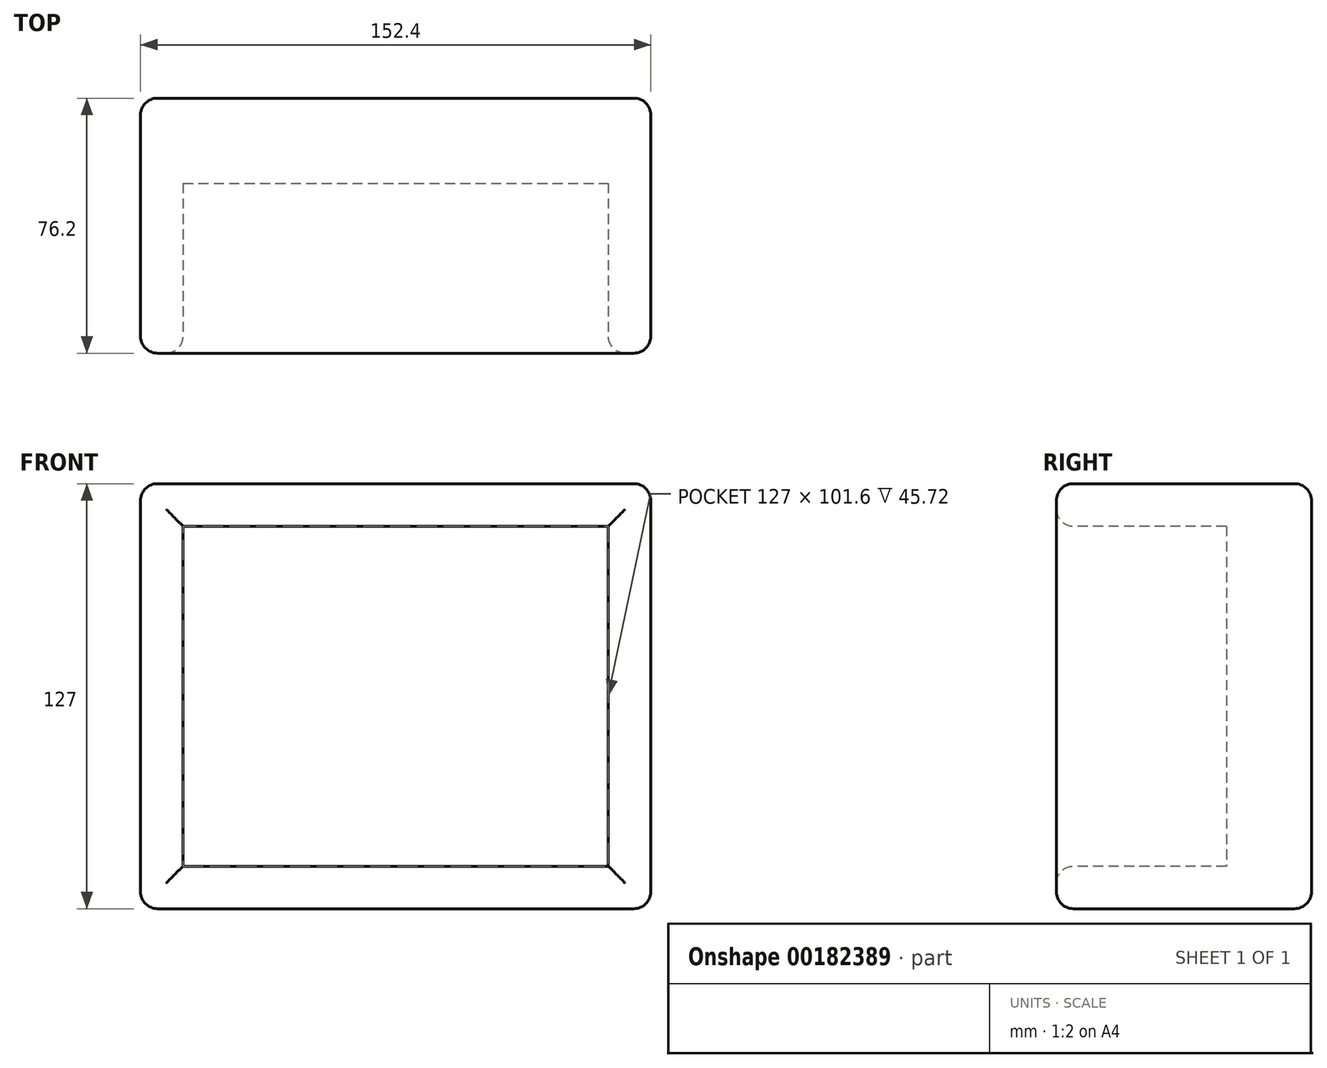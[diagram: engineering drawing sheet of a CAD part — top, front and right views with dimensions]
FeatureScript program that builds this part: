
annotation { "Feature Type Name" : "Feature", "Feature Type Description" : "" }
export const myFeature = defineFeature(function(context is Context, id is Id, definition is map)
    precondition{}
    {
        {
            var Q0;
            Q0=qCreatedBy(makeId("Front.planeOp"),FACE);
            var sketch = newSketch(context, id + "F0", { "sketchPlane" : qUnion([Q0])});
            skLineSegment(sketch, "E0.bottom", {"start": v(76.2, -63.5) * mm, "end": v(-76.2, -63.5) * mm});
            skLineSegment(sketch, "E0.top", {"start": v(76.2, 63.5) * mm, "end": v(-76.2, 63.5) * mm});
            skLineSegment(sketch, "E0.left", {"start": v(76.2, -63.5) * mm, "end": v(76.2, 63.5) * mm});
            skLineSegment(sketch, "E0.right", {"start": v(-76.2, -63.5) * mm, "end": v(-76.2, 63.5) * mm});
            skPoint(sketch, "E0.middle", {"position": v(0, 0) * mm});
            skSolve(sketch);
        }
        {
            var Q0;
            Q0=makeQuery(id+"F0.imprint","IMPRINT",FACE,{"disambiguationData":[TD([[makeQuery(id+"F0.imprint","IMPRINT",EDGE,{"derivedFrom":sQuery(id+"F0.wireOp",EDGE,"E0.bottom")}),-1.0]])]});
            extrude(context, id + "F1", {"entities" : qUnion([Q0]), "oppositeDirection" : true, "depth" : 76.2 * mm});
        }
        {
            var Q0;
            Q0=makeQuery(id+"F1.opExtrude","CAP_FACE",FACE,{"disambiguationData":[OSD([sQuery(id+"F0.wireOp",EDGE,"E0.bottom"),sQuery(id+"F0.wireOp",EDGE,"E0.top"),sQuery(id+"F0.wireOp",EDGE,"E0.left"),sQuery(id+"F0.wireOp",EDGE,"E0.right")])],"isStart":true});
            var sketch = newSketch(context, id + "F2", { "sketchPlane" : qUnion([Q0])});
            skLineSegment(sketch, "E1.bottom", {"start": v(-63.5, 50.8) * mm, "end": v(63.5, 50.8) * mm});
            skLineSegment(sketch, "E1.top", {"start": v(-63.5, -50.8) * mm, "end": v(63.5, -50.8) * mm});
            skLineSegment(sketch, "E1.left", {"start": v(-63.5, 50.8) * mm, "end": v(-63.5, -50.8) * mm});
            skLineSegment(sketch, "E1.right", {"start": v(63.5, 50.8) * mm, "end": v(63.5, -50.8) * mm});
            skPoint(sketch, "E1.middle", {"position": v(0, 0) * mm});
            skSolve(sketch);
        }
        {
            var Q0;
            Q0=makeQuery(id+"F2.imprint","IMPRINT",FACE,{"disambiguationData":[TD([[makeQuery(id+"F2.imprint","IMPRINT",EDGE,{"derivedFrom":sQuery(id+"F2.wireOp",EDGE,"E1.bottom")}),-1.0]])]});
            extrude(context, id + "F3", {"entities" : qUnion([Q0]), "operationType" : NewBodyOperationType.REMOVE, "oppositeDirection" : true, "depth" : 50.8 * mm});
        }
        {
            var Q0;
            Q0=makeQuery(id+"F1.opExtrude","CAP_EDGE",EDGE,{"disambiguationData":[OSD([sQuery(id+"F0.wireOp",EDGE,"E0.right")])],"isStart":true});
            var Q1;
            Q1=makeQuery(id+"F1.opExtrude","CAP_EDGE",EDGE,{"disambiguationData":[OSD([sQuery(id+"F0.wireOp",EDGE,"E0.top")])],"isStart":true});
            var Q2;
            Q2=makeQuery(id+"F3.boolean.opBoolean","COPY",EDGE,{"derivedFrom":makeQuery(id+"F3.opExtrude","CAP_EDGE",EDGE,{"disambiguationData":[OSD([sQuery(id+"F2.wireOp",EDGE,"E1.bottom")])],"isStart":true})});
            var Q3;
            Q3=makeQuery(id+"F3.boolean.opBoolean","COPY",EDGE,{"derivedFrom":makeQuery(id+"F3.opExtrude","CAP_EDGE",EDGE,{"disambiguationData":[OSD([sQuery(id+"F2.wireOp",EDGE,"E1.left")])],"isStart":true})});
            var Q4;
            Q4=makeQuery(id+"F3.boolean.opBoolean","COPY",EDGE,{"derivedFrom":makeQuery(id+"F3.opExtrude","CAP_EDGE",EDGE,{"disambiguationData":[OSD([sQuery(id+"F2.wireOp",EDGE,"E1.top")])],"isStart":true})});
            var Q5;
            Q5=makeQuery(id+"F1.opExtrude","CAP_EDGE",EDGE,{"disambiguationData":[OSD([sQuery(id+"F0.wireOp",EDGE,"E0.bottom")])],"isStart":true});
            var Q6;
            Q6=makeQuery(id+"F1.opExtrude","CAP_FACE",FACE,{"disambiguationData":[OSD([sQuery(id+"F0.wireOp",EDGE,"E0.bottom"),sQuery(id+"F0.wireOp",EDGE,"E0.top"),sQuery(id+"F0.wireOp",EDGE,"E0.left"),sQuery(id+"F0.wireOp",EDGE,"E0.right")])],"isStart":true});
            var Q7;
            Q7=makeQuery(id+"F1.opExtrude","SWEPT_EDGE",EDGE,{"disambiguationData":[OSD([sQuery(id+"F0.wireOp",EDGE,"E0.top"),sQuery(id+"F0.wireOp",EDGE,"E0.left")])]});
            var Q8;
            Q8=makeQuery(id+"F1.opExtrude","CAP_EDGE",EDGE,{"disambiguationData":[OSD([sQuery(id+"F0.wireOp",EDGE,"E0.left")])],"isStart":false});
            var Q9;
            Q9=makeQuery(id+"F1.opExtrude","SWEPT_FACE",FACE,{"disambiguationData":[OSD([sQuery(id+"F0.wireOp",EDGE,"E0.left")])]});
            var Q10;
            Q10=makeQuery(id+"F1.opExtrude","SWEPT_FACE",FACE,{"disambiguationData":[OSD([sQuery(id+"F0.wireOp",EDGE,"E0.top")])]});
            var Q11;
            Q11=makeQuery(id+"F1.opExtrude","SWEPT_FACE",FACE,{"disambiguationData":[OSD([sQuery(id+"F0.wireOp",EDGE,"E0.right")])]});
            var Q12;
            Q12=makeQuery(id+"F1.opExtrude","CAP_FACE",FACE,{"disambiguationData":[OSD([sQuery(id+"F0.wireOp",EDGE,"E0.bottom"),sQuery(id+"F0.wireOp",EDGE,"E0.top"),sQuery(id+"F0.wireOp",EDGE,"E0.left"),sQuery(id+"F0.wireOp",EDGE,"E0.right")])],"isStart":false});
            fillet(context, id + "F4", {"entities" : qUnion([Q0, Q1, Q2, Q3, Q4, Q5, Q6, Q7, Q8, Q9, Q10, Q11, Q12]), "radius" : 5.08 * mm, "tangentPropagation" : true, "allowEdgeOverflow" : false});
        }
    });
